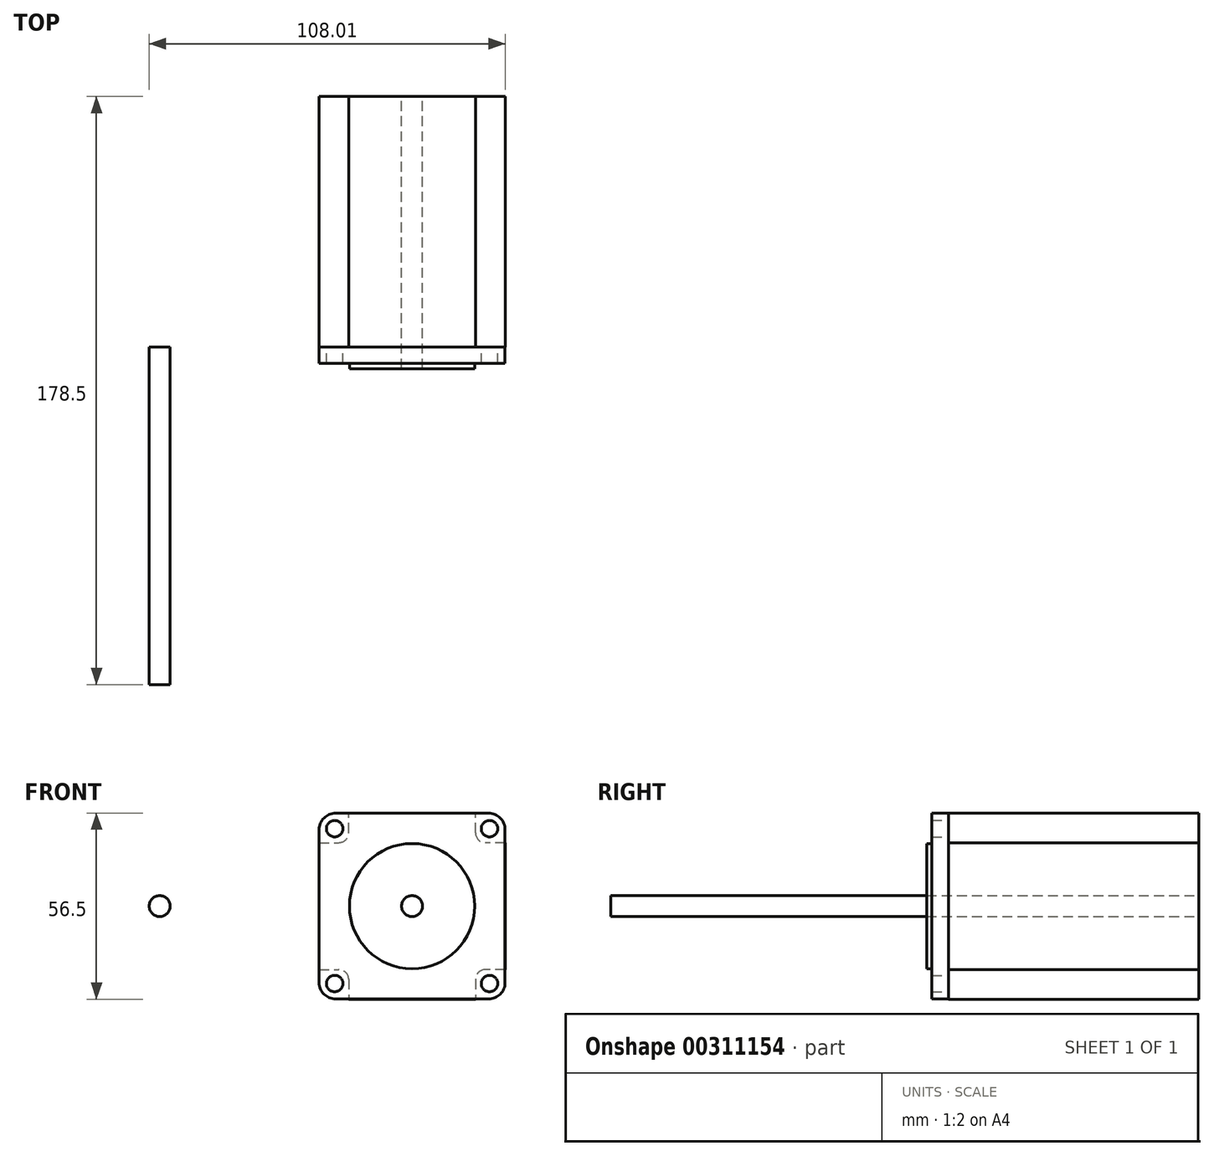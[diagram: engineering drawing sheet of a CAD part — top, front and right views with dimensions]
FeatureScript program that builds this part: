
annotation { "Feature Type Name" : "Feature", "Feature Type Description" : "" }
export const myFeature = defineFeature(function(context is Context, id is Id, definition is map)
    precondition{}
    {
        {
            var Q0;
            Q0=qCreatedBy(makeId("Front.planeOp"),FACE);
            var sketch = newSketch(context, id + "F0", { "sketchPlane" : qUnion([Q0])});
            skLineSegment(sketch, "E0.bottom", {"start": v(-23.2, 28.2) * mm, "end": v(23.2, 28.2) * mm});
            skLineSegment(sketch, "E0.top", {"start": v(-23.2, -28.2) * mm, "end": v(23.2, -28.2) * mm});
            skLineSegment(sketch, "E0.left", {"start": v(-28.2, 23.2) * mm, "end": v(-28.2, -23.2) * mm});
            skLineSegment(sketch, "E0.right", {"start": v(28.2, 23.2) * mm, "end": v(28.2, -23.2) * mm});
            skCircle(sketch, "E1", {"center": v(-23.5, 23.5) * mm, "radius": 2.5 * mm});
            skCircle(sketch, "E2", {"center": v(23.5, 23.5) * mm, "radius": 2.5 * mm});
            skCircle(sketch, "E3", {"center": v(-23.5, -23.5) * mm, "radius": 2.5 * mm});
            skCircle(sketch, "E4", {"center": v(23.5, -23.5) * mm, "radius": 2.5 * mm});
            skPoint(sketch, "E5.visualSharp", {"position": v(-28.2, 28.2) * mm});
            skArc(sketch, "E5.filletArc", {"start": v(-23.2, 28.2) * mm, "mid": v(-26.74, 26.74) * mm, "end": v(-28.2, 23.2) * mm});
            skPoint(sketch, "E6.visualSharp", {"position": v(28.2, 28.2) * mm});
            skArc(sketch, "E6.filletArc", {"start": v(28.2, 23.2) * mm, "mid": v(26.74, 26.74) * mm, "end": v(23.2, 28.2) * mm});
            skPoint(sketch, "E7.visualSharp", {"position": v(28.2, -28.2) * mm});
            skArc(sketch, "E7.filletArc", {"start": v(23.2, -28.2) * mm, "mid": v(26.74, -26.74) * mm, "end": v(28.2, -23.2) * mm});
            skPoint(sketch, "E8.visualSharp", {"position": v(-28.2, -28.2) * mm});
            skArc(sketch, "E8.filletArc", {"start": v(-28.2, -23.2) * mm, "mid": v(-26.74, -26.74) * mm, "end": v(-23.2, -28.2) * mm});
            skCircle(sketch, "E9", {"center": v(0, 0) * mm, "radius": 19 * mm});
            skCircle(sketch, "E10", {"center": v(0, 0) * mm, "radius": 3.17 * mm});
            skCircle(sketch, "E11", {"center": v(-76.58, 0) * mm, "radius": 3.17 * mm});
            skSolve(sketch);
        }
        {
            var Q0;
            Q0=makeQuery(id+"F0.imprint","IMPRINT",FACE,{"disambiguationData":[TD([[makeQuery(id+"F0.imprint","IMPRINT",EDGE,{"derivedFrom":sQuery(id+"F0.wireOp",EDGE,"E0.bottom")}),-1.0]])]});
            extrude(context, id + "F1", {"entities" : qUnion([Q0]), "depth" : 5 * mm});
        }
        {
            var Q0;
            Q0=makeQuery(id+"F0.imprint","IMPRINT",FACE,{"disambiguationData":[TD([[makeQuery(id+"F0.imprint","IMPRINT",EDGE,{"derivedFrom":sQuery(id+"F0.wireOp",EDGE,"E9")}),1.0]])]});
            extrude(context, id + "F2", {"entities" : qUnion([Q0]), "operationType" : NewBodyOperationType.ADD, "depth" : 6.6 * mm});
        }
        {
            var Q0;
            Q0=makeQuery(id+"F0.imprint","IMPRINT",FACE,{"disambiguationData":[TD([[makeQuery(id+"F0.imprint","IMPRINT",EDGE,{"derivedFrom":sQuery(id+"F0.wireOp",EDGE,"E0.bottom")}),-1.0]])]});
            var sketch = newSketch(context, id + "F3", { "sketchPlane" : qUnion([Q0])});
            skLineSegment(sketch, "E12", {"start": v(28.25, 19.25) * mm, "end": v(22.25, 19.25) * mm});
            skLineSegment(sketch, "E13", {"start": v(19.25, 22.25) * mm, "end": v(19.25, 28.25) * mm});
            skPoint(sketch, "E14.visualSharp", {"position": v(19.25, 19.25) * mm});
            skArc(sketch, "E14.filletArc", {"start": v(19.25, 22.25) * mm, "mid": v(20.13, 20.13) * mm, "end": v(22.25, 19.25) * mm});
            skLineSegment(sketch, "E15", {"start": v(0, 5.97) * mm, "end": v(0, 13.85) * mm, "construction": true});
            skLineSegment(sketch, "E16", {"start": v(7.64, 0) * mm, "end": v(14.56, 0) * mm, "construction": true});
            skLineSegment(sketch, "E17.MirrorCS", {"start": v(-28.25, 19.25) * mm, "end": v(-22.25, 19.25) * mm});
            skArc(sketch, "E18.MirrorCS", {"start": v(-19.25, 22.25) * mm, "mid": v(-20.13, 20.13) * mm, "end": v(-22.25, 19.25) * mm});
            skLineSegment(sketch, "E19.MirrorCS", {"start": v(-19.25, 22.25) * mm, "end": v(-19.25, 28.25) * mm});
            skLineSegment(sketch, "E20.MirrorCS", {"start": v(28.25, -19.25) * mm, "end": v(22.25, -19.25) * mm});
            skArc(sketch, "E21.MirrorCS", {"start": v(19.25, -22.25) * mm, "mid": v(20.13, -20.13) * mm, "end": v(22.25, -19.25) * mm});
            skLineSegment(sketch, "E22.MirrorCS", {"start": v(19.25, -22.25) * mm, "end": v(19.25, -28.25) * mm});
            skLineSegment(sketch, "E23.MirrorCS", {"start": v(-28.25, -19.25) * mm, "end": v(-22.25, -19.25) * mm});
            skArc(sketch, "E24.MirrorCS", {"start": v(-19.25, -22.25) * mm, "mid": v(-20.13, -20.13) * mm, "end": v(-22.25, -19.25) * mm});
            skLineSegment(sketch, "E25.MirrorCS", {"start": v(-19.25, -22.25) * mm, "end": v(-19.25, -28.25) * mm});
            skLineSegment(sketch, "E26", {"start": v(19.25, 28.25) * mm, "end": v(-19.25, 28.25) * mm});
            skLineSegment(sketch, "E27", {"start": v(-28.25, 19.25) * mm, "end": v(-28.25, -19.25) * mm});
            skLineSegment(sketch, "E28", {"start": v(-19.25, -28.25) * mm, "end": v(19.25, -28.25) * mm});
            skLineSegment(sketch, "E29", {"start": v(28.25, -19.25) * mm, "end": v(28.25, 19.25) * mm});
            skCircle(sketch, "E30", {"center": v(0, 0) * mm, "radius": 3.17 * mm});
            skSolve(sketch);
        }
        {
            var Q0;
            Q0 = qSketchRegion(id + "F3", true);
            extrude(context, id + "F4", {"entities" : qUnion([Q0]), "operationType" : NewBodyOperationType.ADD, "oppositeDirection" : true, "depth" : 76 * mm});
        }
        {
            var Q0;
            Q0=makeQuery(id+"F0.imprint","IMPRINT",FACE,{"disambiguationData":[TD([[makeQuery(id+"F0.imprint","IMPRINT",EDGE,{"derivedFrom":sQuery(id+"F0.wireOp",EDGE,"E11")}),1.0]])]});
            extrude(context, id + "F5", {"entities" : qUnion([Q0]), "depth" : 102.5 * mm});
        }
    });
